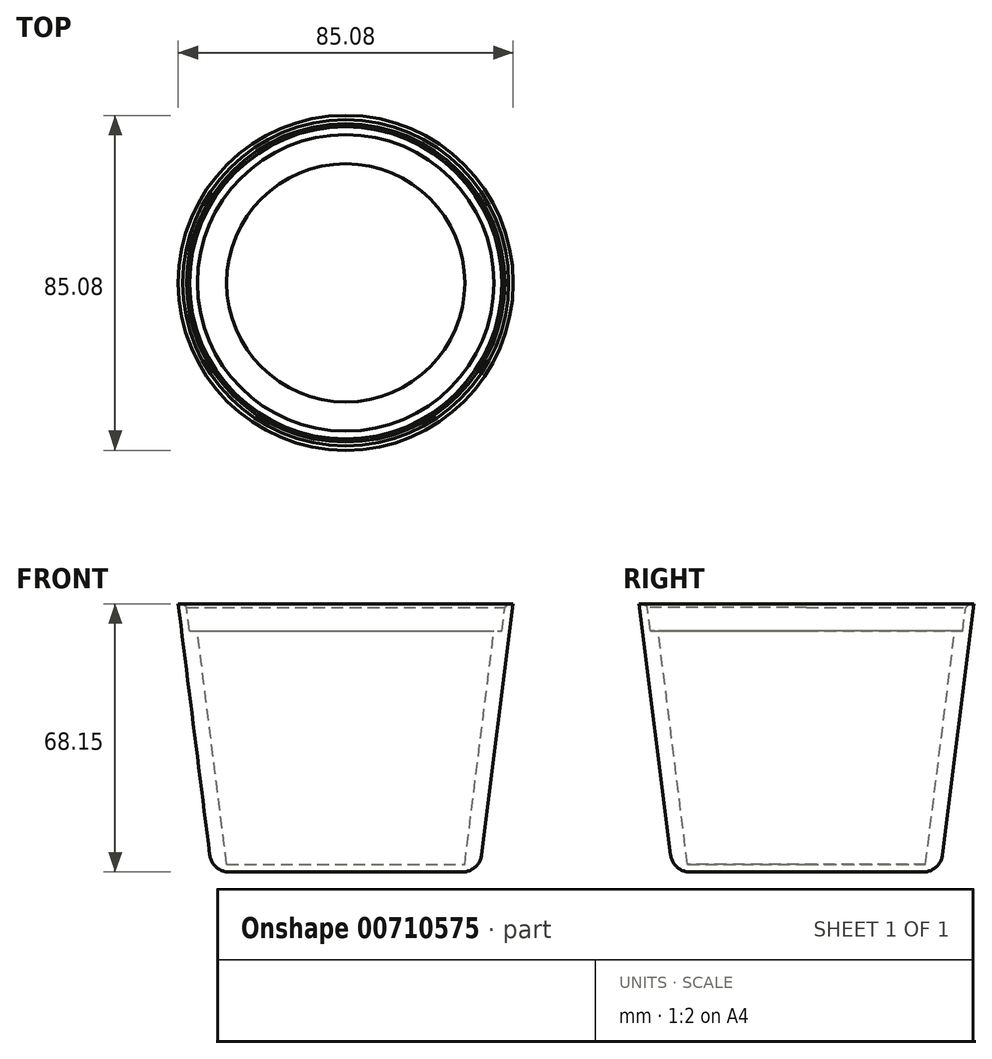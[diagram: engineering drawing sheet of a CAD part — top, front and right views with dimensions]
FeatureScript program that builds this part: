
annotation { "Feature Type Name" : "Feature", "Feature Type Description" : "" }
export const myFeature = defineFeature(function(context is Context, id is Id, definition is map)
    precondition{}
    {
        {
            var Q0;
            Q0=qCreatedBy(makeId("Front.planeOp"),FACE);
            var sketch = newSketch(context, id + "F0", { "sketchPlane" : qUnion([Q0])});
            skLineSegment(sketch, "E0", {"start": v(0, 76.77) * mm, "end": v(0, 79.77) * mm});
            skLineSegment(sketch, "E1", {"start": v(0, 79.77) * mm, "end": v(-44, 79.77) * mm});
            skLineSegment(sketch, "E2", {"start": v(-44, 79.77) * mm, "end": v(-34, 0) * mm});
            skLineSegment(sketch, "E3", {"start": v(-34, 0) * mm, "end": v(0, 0) * mm});
            skLineSegment(sketch, "E4", {"start": v(0, 0) * mm, "end": v(0, 2) * mm});
            skLineSegment(sketch, "E5", {"start": v(0, 2) * mm, "end": v(-30.25, 2) * mm});
            skLineSegment(sketch, "E6", {"start": v(-30.25, 2) * mm, "end": v(-39.62, 76.77) * mm});
            skLineSegment(sketch, "E7", {"start": v(-39.62, 76.77) * mm, "end": v(0, 76.77) * mm});
            skLineSegment(sketch, "E8", {"start": v(-42.54, 68.15) * mm, "end": v(-40.54, 68.15) * mm});
            skLineSegment(sketch, "E9", {"start": v(-40.54, 68.15) * mm, "end": v(-39.67, 61.2) * mm});
            skLineSegment(sketch, "E10", {"start": v(-39.67, 61.2) * mm, "end": v(-37.67, 61.2) * mm});
            skLineSegment(sketch, "E11.0", {"start": v(-39.4, 61.5) * mm, "end": v(-37.71, 61.5) * mm});
            skLineSegment(sketch, "E11.1", {"start": v(-40.28, 68.45) * mm, "end": v(-39.4, 61.5) * mm});
            skLineSegment(sketch, "E11.2", {"start": v(-42.58, 68.45) * mm, "end": v(-40.28, 68.45) * mm});
            skSolve(sketch);
        }
        {
            var Q0;
            {var subQ1=sQuery(id+"F0.wireOp",EDGE,"E3");Q0=makeQuery(id+"F0.imprint","IMPRINT",FACE,{"disambiguationData":[TD([[makeQuery(id+"F0.imprint","IMPRINT",EDGE,{"derivedFrom":subQ1}),1.0]])]});}
            var Q1;
            Q1=makeQuery(id+"F0.imprint","IMPRINT",FACE,{"disambiguationData":[TD([[makeQuery(id+"F0.imprint","IMPRINT",EDGE,{"derivedFrom":sQuery(id+"F0.wireOp",EDGE,"E0")}),1.0]])]});
            var Q2;
            Q2=sQuery(id+"F0.wireOp",EDGE,"E4");
            revolve(context, id + "F1", {"surfaceOperationType" : NewSurfaceOperationType.NEW, "entities" : qUnion([Q0, Q1]), "axis" : qUnion([Q2]), "revolveType" : RevolveType.FULL});
        }
        {
            var Q0;
            Q0=makeQuery(id+"F1.opRevolve","SWEPT_FACE",FACE,{"disambiguationData":[OSD([sQuery(id+"F0.wireOp",EDGE,"E3")])]});
            fillet(context, id + "F2", {"entities" : qUnion([Q0]), "radius" : 5 * mm, "tangentPropagation" : true, "allowEdgeOverflow" : false});
        }
        {
            var Q0;
            Q0=makeQuery(id+"F1.opRevolve","SWEPT_EDGE",EDGE,{"disambiguationData":[OSD([sQuery(id+"F0.wireOp",EDGE,"E8"),sQuery(id+"F0.wireOp",EDGE,"E9")])]});
            chamfer(context, id + "F3", {"entities" : qUnion([Q0]), "width" : 1 * mm, "tangentPropagation" : true});
        }
        {
            var Q0;
            Q0=makeQuery(id+"F1.opRevolve","SWEPT_BODY",BODY,{"disambiguationData":[OSD([sQuery(id+"F0.wireOp",EDGE,"E0"),sQuery(id+"F0.wireOp",EDGE,"E1"),sQuery(id+"F0.wireOp",EDGE,"E2"),sQuery(id+"F0.wireOp",EDGE,"E6"),sQuery(id+"F0.wireOp",EDGE,"E7"),sQuery(id+"F0.wireOp",EDGE,"E11.0"),sQuery(id+"F0.wireOp",EDGE,"E11.1"),sQuery(id+"F0.wireOp",EDGE,"E11.2")])]});
            deleteBodies(context, id + "F4", {"entities" : qUnion([Q0])});
        }
    });
